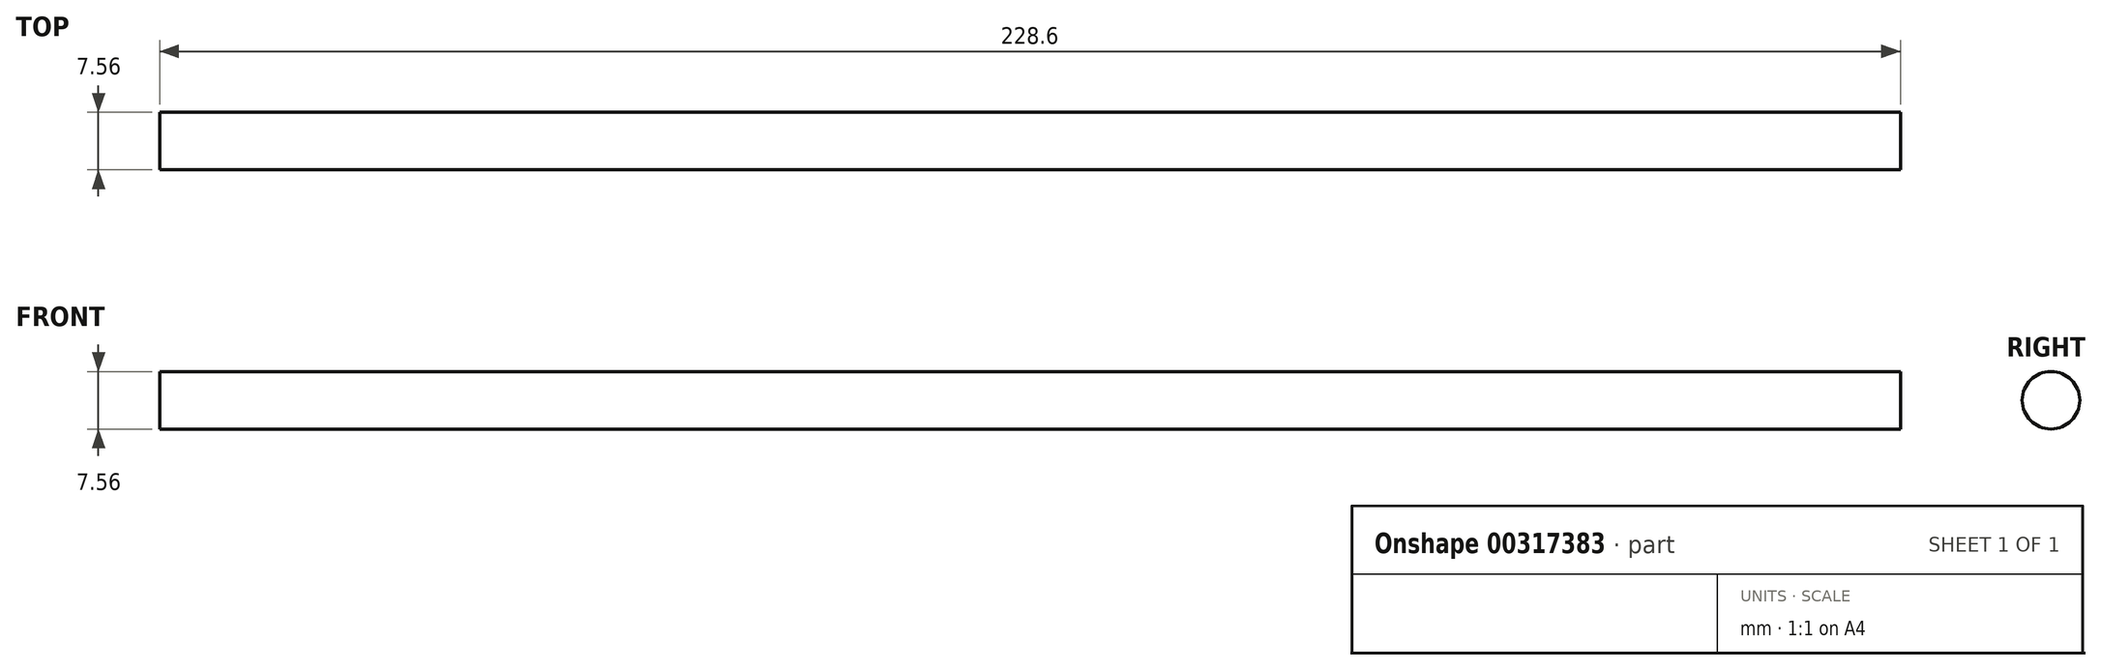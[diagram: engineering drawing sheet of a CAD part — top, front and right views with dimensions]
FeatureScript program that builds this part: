
annotation { "Feature Type Name" : "Feature", "Feature Type Description" : "" }
export const myFeature = defineFeature(function(context is Context, id is Id, definition is map)
    precondition{}
    {
        {
            var Q0;
            Q0=qCreatedBy(makeId("Right.planeOp"),FACE);
            var sketch = newSketch(context, id + "F0", { "sketchPlane" : qUnion([Q0])});
            skCircle(sketch, "E0", {"center": v(0, 0) * mm, "radius": 3.78 * mm});
            skSolve(sketch);
        }
        {
            var Q0;
            Q0 = qSketchRegion(id + "F0", true);
            extrude(context, id + "F1", {"entities" : qUnion([Q0]), "depth" : 228.6 * mm});
        }
    });
